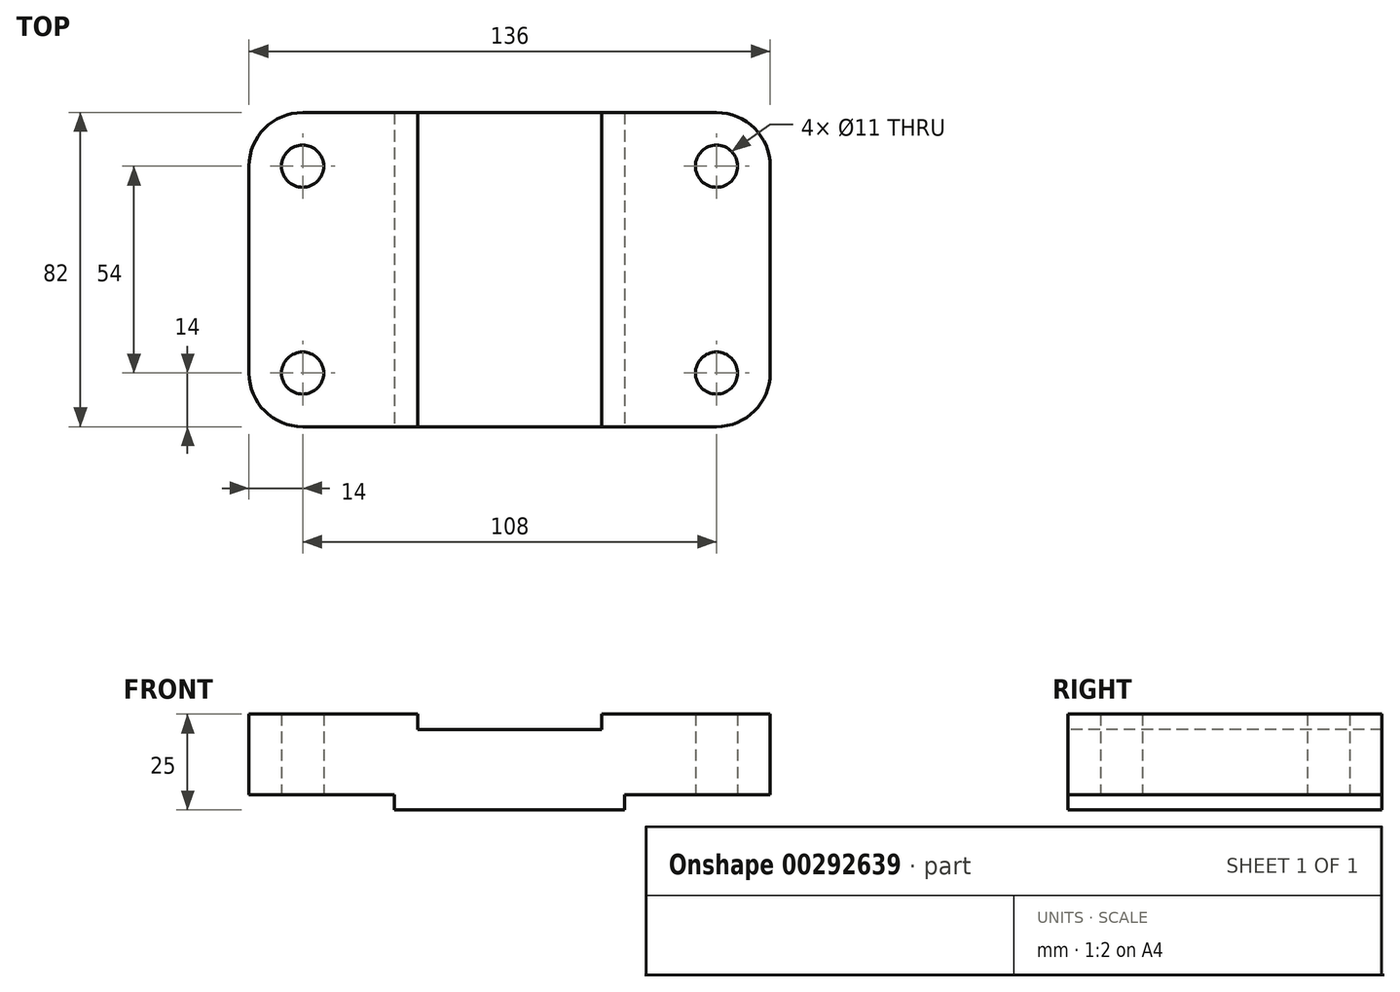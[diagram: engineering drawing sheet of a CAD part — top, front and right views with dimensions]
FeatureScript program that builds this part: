
annotation { "Feature Type Name" : "Feature", "Feature Type Description" : "" }
export const myFeature = defineFeature(function(context is Context, id is Id, definition is map)
    precondition{}
    {
        {
            var Q0;
            Q0=qCreatedBy(makeId("Top.planeOp"),FACE);
            var sketch = newSketch(context, id + "F0", { "sketchPlane" : qUnion([Q0])});
            skLineSegment(sketch, "E0", {"start": v(14, 0) * mm, "end": v(122, 0) * mm});
            skLineSegment(sketch, "E1", {"start": v(136, 14) * mm, "end": v(136, 68) * mm});
            skLineSegment(sketch, "E2", {"start": v(122, 82) * mm, "end": v(14, 82) * mm});
            skLineSegment(sketch, "E3", {"start": v(0, 68) * mm, "end": v(0, 14) * mm});
            skPoint(sketch, "E4.visualSharp", {"position": v(0, 0) * mm});
            skArc(sketch, "E4.filletArc", {"start": v(0, 14) * mm, "mid": v(4.1, 4.1) * mm, "end": v(14, 0) * mm});
            skPoint(sketch, "E5.visualSharp", {"position": v(0, 82) * mm});
            skArc(sketch, "E5.filletArc", {"start": v(14, 82) * mm, "mid": v(4.1, 77.9) * mm, "end": v(0, 68) * mm});
            skPoint(sketch, "E6.visualSharp", {"position": v(136, 82) * mm});
            skArc(sketch, "E6.filletArc", {"start": v(136, 68) * mm, "mid": v(131.9, 77.9) * mm, "end": v(122, 82) * mm});
            skPoint(sketch, "E7.visualSharp", {"position": v(136, 0) * mm});
            skArc(sketch, "E7.filletArc", {"start": v(122, 0) * mm, "mid": v(131.9, 4.1) * mm, "end": v(136, 14) * mm});
            skCircle(sketch, "E8", {"center": v(14, 68) * mm, "radius": 5.5 * mm});
            skCircle(sketch, "E9", {"center": v(122, 68) * mm, "radius": 5.5 * mm});
            skCircle(sketch, "E10", {"center": v(122, 14) * mm, "radius": 5.5 * mm});
            skCircle(sketch, "E11", {"center": v(14, 14) * mm, "radius": 5.5 * mm});
            skLineSegment(sketch, "E12", {"start": v(14, 68) * mm, "end": v(14, 14) * mm, "construction": true});
            skLineSegment(sketch, "E13", {"start": v(14, 68) * mm, "end": v(122, 68) * mm, "construction": true});
            skLineSegment(sketch, "E14", {"start": v(122, 14) * mm, "end": v(122, 68) * mm, "construction": true});
            skLineSegment(sketch, "E15", {"start": v(14, 14) * mm, "end": v(122, 14) * mm, "construction": true});
            skLineSegment(sketch, "E16", {"start": v(45.3, 82) * mm, "end": v(45.3, 0) * mm});
            skLineSegment(sketch, "E17", {"start": v(90.7, 82) * mm, "end": v(90.7, 0) * mm});
            skSolve(sketch);
        }
        {
            var Q0;
            Q0 = qSketchRegion(id + "F0", true);
            extrude(context, id + "F1", {"entities" : qUnion([Q0]), "depth" : 25 * mm});
        }
        {
            var Q0;
            Q0=makeQuery(id+"F1.opExtrude","SWEPT_FACE",FACE,{"disambiguationData":[OSD([sQuery(id+"F0.wireOp",EDGE,"E0")])]});
            var sketch = newSketch(context, id + "F2", { "sketchPlane" : qUnion([Q0])});
            skLineSegment(sketch, "E18", {"start": v(44, 25) * mm, "end": v(92, 25) * mm});
            skLineSegment(sketch, "E19", {"start": v(44, 25) * mm, "end": v(44, 21) * mm});
            skLineSegment(sketch, "E20", {"start": v(44, 21) * mm, "end": v(92, 21) * mm});
            skLineSegment(sketch, "E21", {"start": v(92, 21) * mm, "end": v(92, 25) * mm});
            skLineSegment(sketch, "E22.bottom", {"start": v(0, 0) * mm, "end": v(38, 0) * mm});
            skLineSegment(sketch, "E22.top", {"start": v(0, 4) * mm, "end": v(38, 4) * mm});
            skLineSegment(sketch, "E22.left", {"start": v(0, 0) * mm, "end": v(0, 4) * mm});
            skLineSegment(sketch, "E22.right", {"start": v(38, 0) * mm, "end": v(38, 4) * mm});
            skLineSegment(sketch, "E23.bottom", {"start": v(136, 0) * mm, "end": v(98, 0) * mm});
            skLineSegment(sketch, "E23.top", {"start": v(136, 4) * mm, "end": v(98, 4) * mm});
            skLineSegment(sketch, "E23.left", {"start": v(136, 0) * mm, "end": v(136, 4) * mm});
            skLineSegment(sketch, "E23.right", {"start": v(98, 0) * mm, "end": v(98, 4) * mm});
            skSolve(sketch);
        }
        {
            var Q0;
            Q0 = qSketchRegion(id + "F2", true);
            extrude(context, id + "F3", {"entities" : qUnion([Q0]), "operationType" : NewBodyOperationType.REMOVE, "endBound" : BoundingType.THROUGH_ALL, "oppositeDirection" : true, "depth" : 25 * mm});
        }
    });
